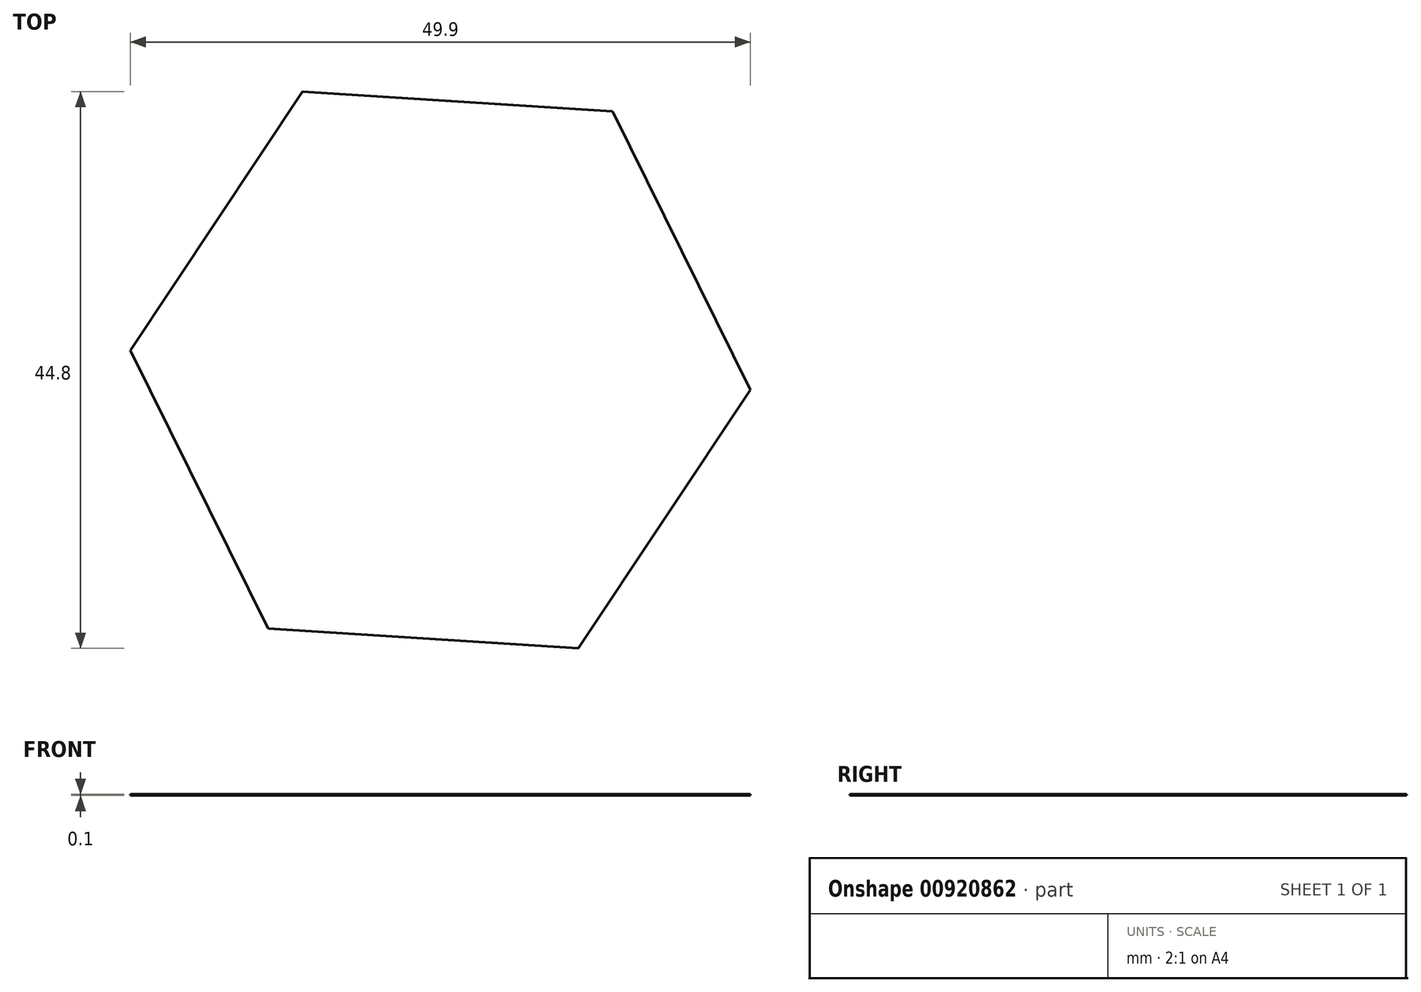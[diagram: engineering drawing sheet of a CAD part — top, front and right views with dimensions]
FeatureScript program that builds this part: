
annotation { "Feature Type Name" : "Feature", "Feature Type Description" : "" }
export const myFeature = defineFeature(function(context is Context, id is Id, definition is map)
    precondition{}
    {
        {
            assignVariable(context, id + "F0", {"name" : "e", "anyValue" : 0.1});
        }
        {
            var Q0;
            Q0=qCreatedBy(makeId("Top.planeOp"),FACE);
            var sketch = newSketch(context, id + "F1", { "sketchPlane" : qUnion([Q0])});
            skCircle(sketch, "E0.cCircle", {"center": v(0, 0) * mm, "radius": 21.65 * mm, "construction": true});
            skLineSegment(sketch, "E0.0", {"start": v(13.85, 20.81) * mm, "end": v(24.95, -1.59) * mm});
            skLineSegment(sketch, "E0.1", {"start": v(24.95, -1.59) * mm, "end": v(11.1, -22.4) * mm});
            skLineSegment(sketch, "E0.2", {"start": v(11.1, -22.4) * mm, "end": v(-13.85, -20.81) * mm});
            skLineSegment(sketch, "E0.3", {"start": v(-13.85, -20.81) * mm, "end": v(-24.95, 1.59) * mm});
            skLineSegment(sketch, "E0.4", {"start": v(-24.95, 1.59) * mm, "end": v(-11.1, 22.4) * mm});
            skLineSegment(sketch, "E0.5", {"start": v(-11.1, 22.4) * mm, "end": v(13.85, 20.81) * mm});
            skPoint(sketch, "E0.0.midPoint", {"position": v(19.4, 9.61) * mm});
            skSolve(sketch);
        }
        {
            var Q0;
            Q0=makeQuery(id+"F1.imprint","IMPRINT",FACE,{"disambiguationData":[TD([[makeQuery(id+"F1.imprint","IMPRINT",EDGE,{"derivedFrom":sQuery(id+"F1.wireOp",EDGE,"E0.0")}),-1.0]])]});
            extrude(context, id + "F2", {"entities" : qUnion([Q0]), "depth" : (getVariable(context, 'e')) * mm, "offsetDistance" : 25 * mm});
        }
    });
